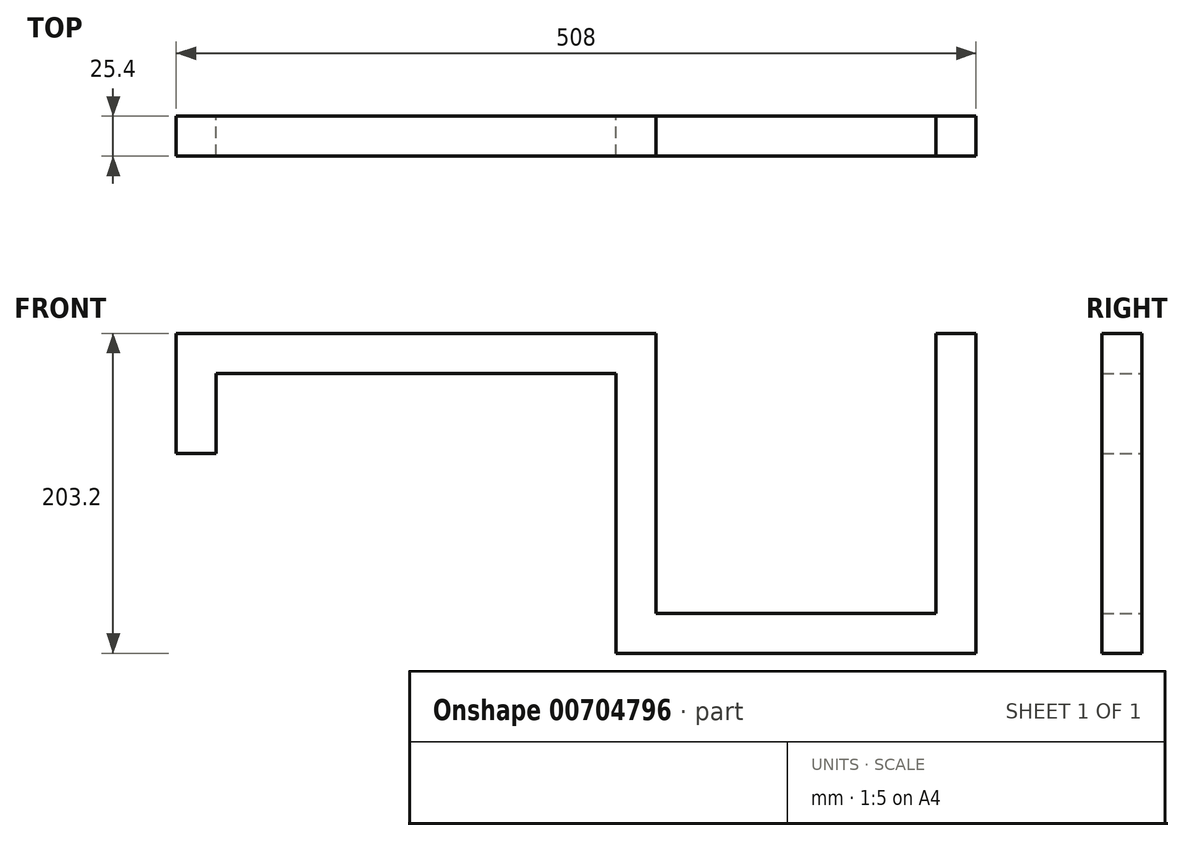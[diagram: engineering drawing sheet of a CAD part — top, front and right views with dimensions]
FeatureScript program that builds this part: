
annotation { "Feature Type Name" : "Feature", "Feature Type Description" : "" }
export const myFeature = defineFeature(function(context is Context, id is Id, definition is map)
    precondition{}
    {
        {
            var Q0;
            Q0=qCreatedBy(makeId("Front.planeOp"),FACE);
            var sketch = newSketch(context, id + "F0", { "sketchPlane" : qUnion([Q0])});
            skLineSegment(sketch, "E0.bottom", {"start": v(127, -12.7) * mm, "end": v(-127, -12.7) * mm});
            skLineSegment(sketch, "E0.top", {"start": v(127, 12.7) * mm, "end": v(-127, 12.7) * mm});
            skLineSegment(sketch, "E0.left", {"start": v(127, -12.7) * mm, "end": v(127, 12.7) * mm});
            skLineSegment(sketch, "E0.right", {"start": v(-127, -12.7) * mm, "end": v(-127, 12.7) * mm});
            skPoint(sketch, "E0.middle", {"position": v(0, 0) * mm});
            skLineSegment(sketch, "E1.bottom", {"start": v(-127, 12.7) * mm, "end": v(-152.4, 12.7) * mm});
            skLineSegment(sketch, "E1.top", {"start": v(-127, -63.5) * mm, "end": v(-152.4, -63.5) * mm});
            skLineSegment(sketch, "E1.left", {"start": v(-127, 12.7) * mm, "end": v(-127, -63.5) * mm});
            skLineSegment(sketch, "E1.right", {"start": v(-152.4, 12.7) * mm, "end": v(-152.4, -63.5) * mm});
            skLineSegment(sketch, "E2.bottom", {"start": v(127, 12.7) * mm, "end": v(152.4, 12.7) * mm});
            skLineSegment(sketch, "E2.top", {"start": v(127, -190.5) * mm, "end": v(152.4, -190.5) * mm});
            skLineSegment(sketch, "E2.left", {"start": v(127, 12.7) * mm, "end": v(127, -190.5) * mm});
            skLineSegment(sketch, "E2.right", {"start": v(152.4, 12.7) * mm, "end": v(152.4, -190.5) * mm});
            skLineSegment(sketch, "E3.bottom", {"start": v(152.4, -190.5) * mm, "end": v(330.2, -190.5) * mm});
            skLineSegment(sketch, "E3.top", {"start": v(152.4, -165.1) * mm, "end": v(330.2, -165.1) * mm});
            skLineSegment(sketch, "E3.left", {"start": v(152.4, -190.5) * mm, "end": v(152.4, -165.1) * mm});
            skLineSegment(sketch, "E3.right", {"start": v(330.2, -190.5) * mm, "end": v(330.2, -165.1) * mm});
            skLineSegment(sketch, "E4.bottom", {"start": v(330.2, -190.5) * mm, "end": v(355.6, -190.5) * mm});
            skLineSegment(sketch, "E4.top", {"start": v(330.2, 12.7) * mm, "end": v(355.6, 12.7) * mm});
            skLineSegment(sketch, "E4.left", {"start": v(330.2, -190.5) * mm, "end": v(330.2, 12.7) * mm});
            skLineSegment(sketch, "E4.right", {"start": v(355.6, -190.5) * mm, "end": v(355.6, 12.7) * mm});
            skSolve(sketch);
        }
        {
            var Q0;
            Q0 = qSketchRegion(id + "F0", true);
            extrude(context, id + "F1", {"entities" : qUnion([Q0]), "depth" : 25.4 * mm, "offsetDistance" : 25.4 * mm});
        }
    });
